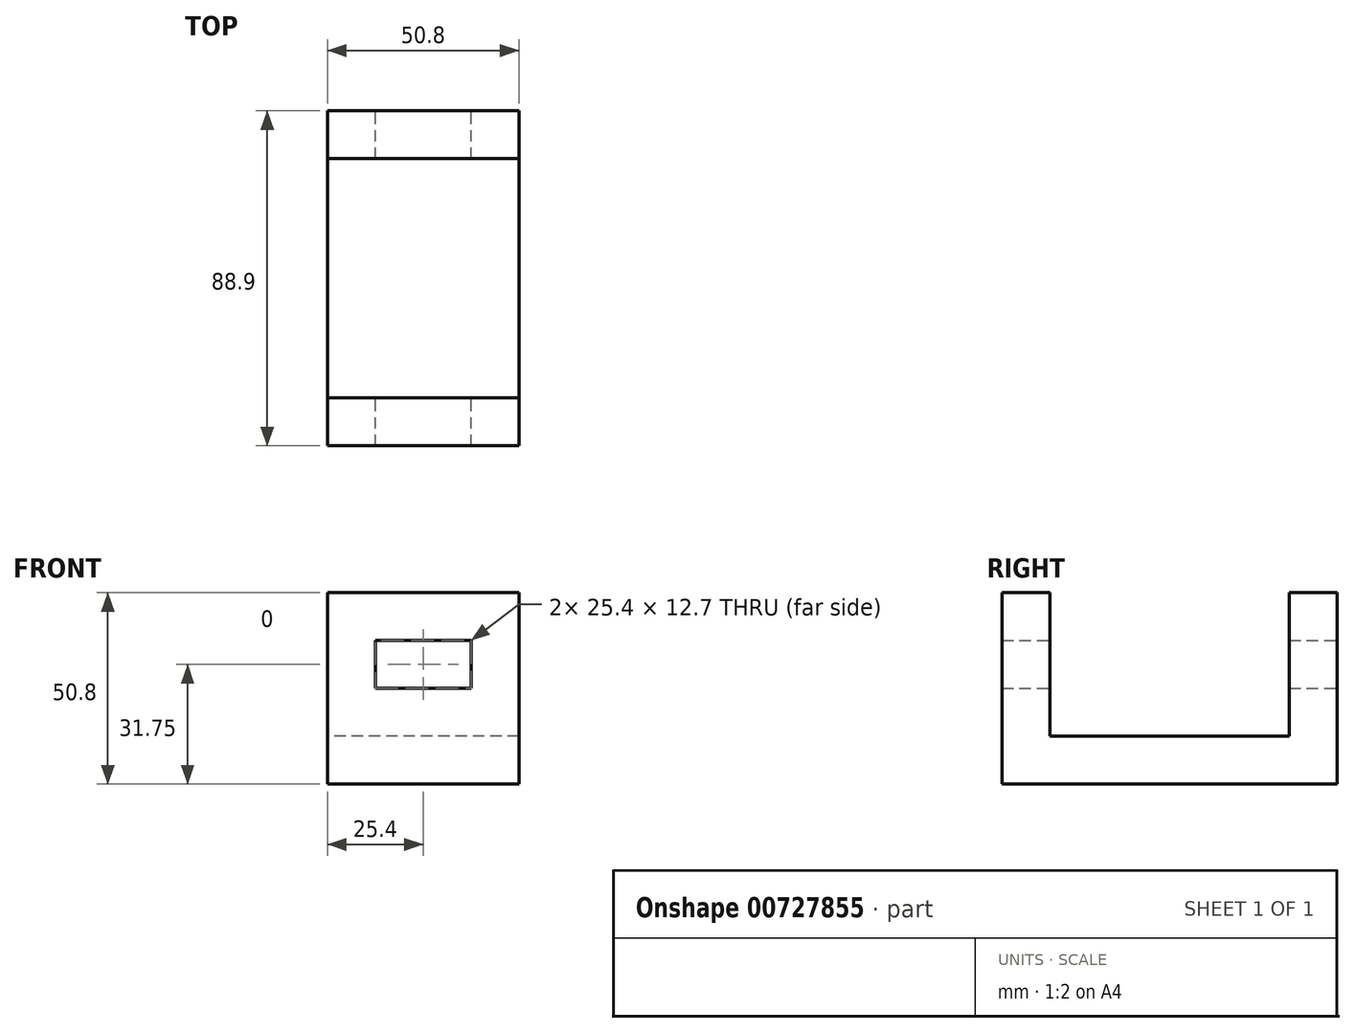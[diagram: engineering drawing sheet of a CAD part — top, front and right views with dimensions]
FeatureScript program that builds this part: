
annotation { "Feature Type Name" : "Feature", "Feature Type Description" : "" }
export const myFeature = defineFeature(function(context is Context, id is Id, definition is map)
    precondition{}
    {
        {
            var Q0;
            Q0=qCreatedBy(makeId("Right.planeOp"),FACE);
            var sketch = newSketch(context, id + "F0", { "sketchPlane" : qUnion([Q0])});
            skLineSegment(sketch, "E0.bottom", {"start": v(86.08, 35.75) * mm, "end": v(98.78, 35.75) * mm});
            skLineSegment(sketch, "E0.top", {"start": v(86.08, -15.05) * mm, "end": v(98.78, -15.05) * mm});
            skLineSegment(sketch, "E0.left", {"start": v(86.08, 35.75) * mm, "end": v(86.08, -2.35) * mm});
            skLineSegment(sketch, "E0.right", {"start": v(98.78, 35.75) * mm, "end": v(98.78, -15.05) * mm});
            skLineSegment(sketch, "E1.bottom", {"start": v(86.08, -15.05) * mm, "end": v(22.58, -15.05) * mm});
            skLineSegment(sketch, "E1.top", {"start": v(86.08, -2.35) * mm, "end": v(22.58, -2.35) * mm});
            skLineSegment(sketch, "E2.bottom", {"start": v(22.58, -15.05) * mm, "end": v(9.88, -15.05) * mm});
            skLineSegment(sketch, "E2.top", {"start": v(22.58, 35.75) * mm, "end": v(9.88, 35.75) * mm});
            skLineSegment(sketch, "E2.left", {"start": v(22.58, -2.35) * mm, "end": v(22.58, 35.75) * mm});
            skLineSegment(sketch, "E2.right", {"start": v(9.88, -15.05) * mm, "end": v(9.88, 35.75) * mm});
            skSolve(sketch);
        }
        {
            var Q0;
            Q0=makeQuery(id+"F0.imprint","IMPRINT",FACE,{"disambiguationData":[TD([[makeQuery(id+"F0.imprint","IMPRINT",EDGE,{"derivedFrom":sQuery(id+"F0.wireOp",EDGE,"E0.bottom")}),-1.0]])]});
            extrude(context, id + "F1", {"entities" : qUnion([Q0]), "depth" : 50.8 * mm, "offsetDistance" : 25.4 * mm});
        }
        {
            var Q0;
            Q0=makeQuery(id+"F1.opExtrude","SWEPT_FACE",FACE,{"disambiguationData":[OSD([sQuery(id+"F0.wireOp",EDGE,"E0.right")])]});
            var sketch = newSketch(context, id + "F2", { "sketchPlane" : qUnion([Q0])});
            skLineSegment(sketch, "E3.bottom", {"start": v(-38.1, 23.05) * mm, "end": v(-12.7, 23.05) * mm});
            skLineSegment(sketch, "E3.top", {"start": v(-38.1, 10.35) * mm, "end": v(-12.7, 10.35) * mm});
            skLineSegment(sketch, "E3.left", {"start": v(-38.1, 23.05) * mm, "end": v(-38.1, 10.35) * mm});
            skLineSegment(sketch, "E3.right", {"start": v(-12.7, 23.05) * mm, "end": v(-12.7, 10.35) * mm});
            skSolve(sketch);
        }
        {
            var Q0;
            Q0=makeQuery(id+"F2.imprint","IMPRINT",FACE,{"disambiguationData":[TD([[makeQuery(id+"F2.imprint","IMPRINT",EDGE,{"derivedFrom":sQuery(id+"F2.wireOp",EDGE,"E3.bottom")}),-1.0]])]});
            extrude(context, id + "F3", {"entities" : qUnion([Q0]), "operationType" : NewBodyOperationType.REMOVE, "oppositeDirection" : true, "depth" : 88.9 * mm, "offsetDistance" : 25.4 * mm});
        }
    });
